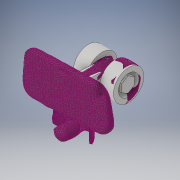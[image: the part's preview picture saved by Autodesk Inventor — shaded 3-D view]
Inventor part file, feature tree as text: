
AUTODESK INVENTOR PART (.ipt)
format: ipt  version: 2017 (Build 210142000, 142)  size: 654,848 bytes
history: native  units: in
note: dims shown in document units (in); Inventor stores cm internally (conversion verified against a paired STEP export)
features: extrude x5, sketch x5, other x4, plane x2, projected_geometry x1
ambient origin geometry x8: Origin, YZ Plane, XZ Plane, XY Plane, X Axis, Y Axis, Z Axis, Center Point
bodies: Solid1 (feature_tree)
feature tree (17):
  other  "rear_mesh"
  plane  "Work Plane1"
  extrude  "Wheel"  Depth=1.5748in
  extrude  "Screw_head"  Depth=1.063in
  other  "Form2"
  plane  "Work Plane2"
  extrude  "Wheel2"  Depth=0.7874in
  extrude  "Extrusion4"  [1 undecoded]
  extrude  "Extrusion5"  Depth=0.3937in
  sketch  "Sketch1"  dims[d0=0.7874in d1=1.5748in]
  sketch  "Sketch3"  dims[d2=0.1575in d3=1.063in]
  sketch  "Sketch4"  dims[d4=0.7087in d5=0.0in d6=0.7874in]
  projected_geometry  "Projected Loop1"
  sketch  "Sketch5"  dims[d7=0.6299in d8=0.0in d9=-0.5906in]
  sketch  "Sketch6"  dims[d10=0.7087in d11=0.0in d12=0.6693in d13=0.5906in d14=0.6299in d15=0.0in d16=0.3937in d17=0.088in d18=0.0206in d19=0.0057in d20=0.6491in d21=0.3849in d22=0.3937in d23=0.6299in d24=0.3937in d25=0.1969in d26=0.0in d27=0.0in]
  other  "MeshFeature1"
  other  "Srf3"
note: 1 required parameter value undecoded (feature->parameter linkage not recoverable at this tier; creation-order binding heuristic only, values carry confidence <= 0.55)
